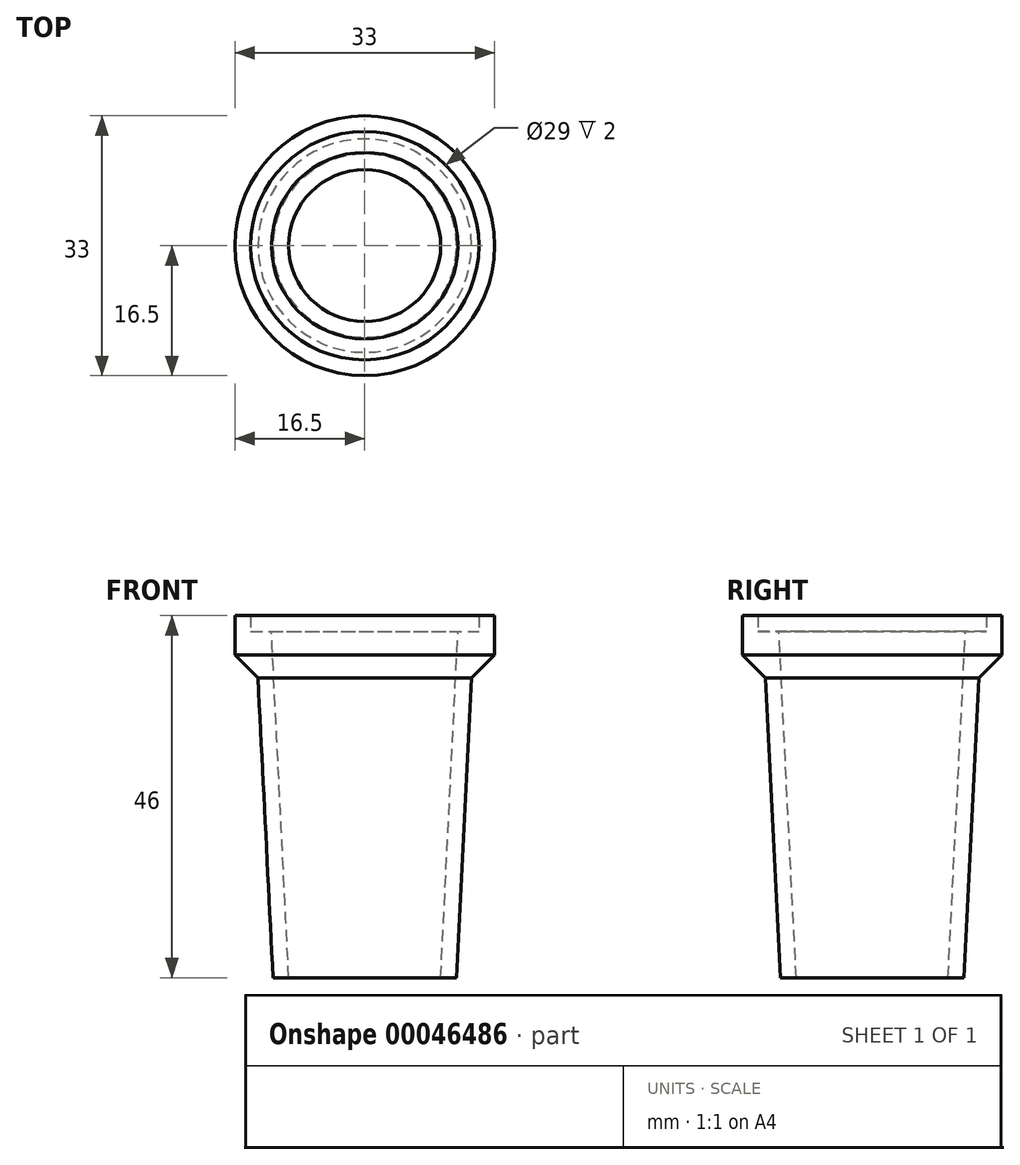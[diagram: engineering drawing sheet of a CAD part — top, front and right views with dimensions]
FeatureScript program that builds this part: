
annotation { "Feature Type Name" : "Feature", "Feature Type Description" : "" }
export const myFeature = defineFeature(function(context is Context, id is Id, definition is map)
    precondition{}
    {
        {
            var Q0;
            Q0=qCreatedBy(makeId("Front.planeOp"),FACE);
            var sketch = newSketch(context, id + "F0", { "sketchPlane" : qUnion([Q0])});
            skLineSegment(sketch, "E0", {"start": v(-9.65, 0) * mm, "end": v(-11.65, 0) * mm});
            skLineSegment(sketch, "E1", {"start": v(-11.65, 0) * mm, "end": v(-13.56, 38.06) * mm});
            skLineSegment(sketch, "E2", {"start": v(-16.5, 41) * mm, "end": v(-13.56, 38.06) * mm});
            skLineSegment(sketch, "E3", {"start": v(-16.5, 41) * mm, "end": v(-16.5, 46) * mm});
            skLineSegment(sketch, "E4", {"start": v(-16.5, 46) * mm, "end": v(-14.5, 46) * mm});
            skLineSegment(sketch, "E5", {"start": v(-14.5, 46) * mm, "end": v(-14.5, 44) * mm});
            skLineSegment(sketch, "E6", {"start": v(-14.5, 44) * mm, "end": v(-11.85, 44) * mm});
            skLineSegment(sketch, "E7", {"start": v(-11.85, 44) * mm, "end": v(-9.65, 0) * mm});
            skLineSegment(sketch, "E8", {"start": v(0, 0) * mm, "end": v(0, 44) * mm, "construction": true});
            skSolve(sketch);
        }
        {
            var Q0;
            Q0 = qSketchRegion(id + "F0", true);
            var Q1;
            Q1=sQuery(id+"F0.wireOp",EDGE,"E8");
            revolve(context, id + "F1", {"entities" : qUnion([Q0]), "axis" : qUnion([Q1]), "revolveType" : RevolveType.FULL});
        }
    });
